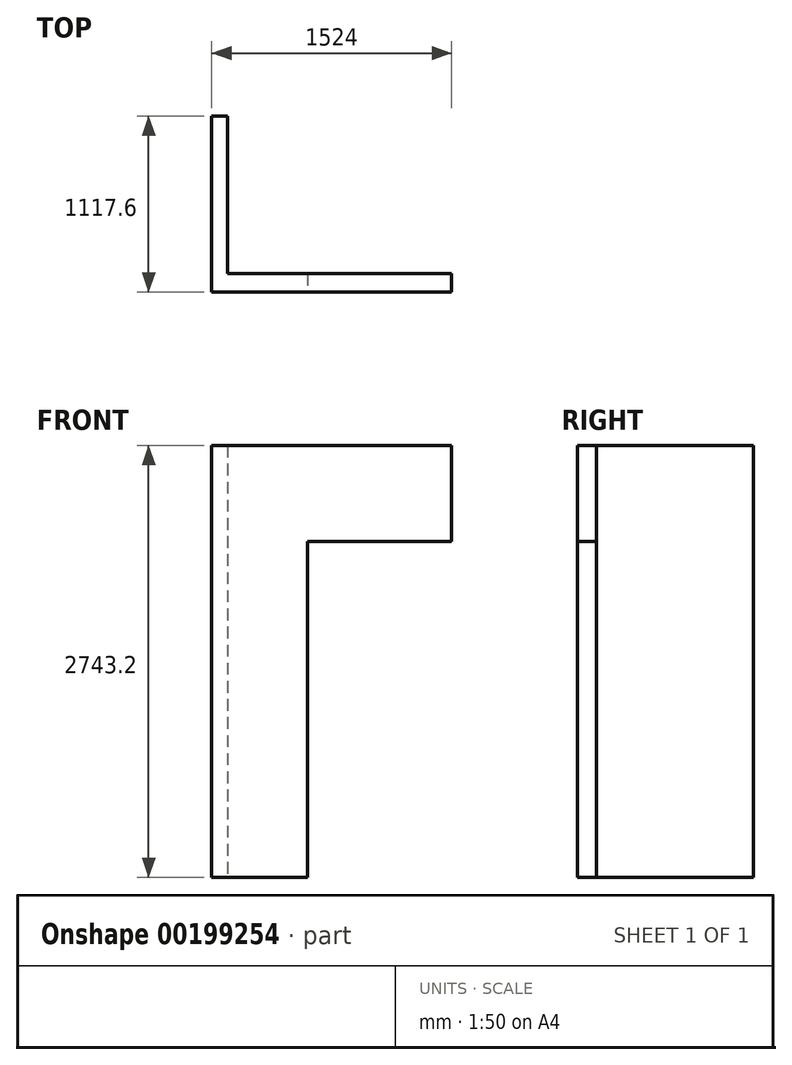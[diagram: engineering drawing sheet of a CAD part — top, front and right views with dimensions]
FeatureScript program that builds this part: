
annotation { "Feature Type Name" : "Feature", "Feature Type Description" : "" }
export const myFeature = defineFeature(function(context is Context, id is Id, definition is map)
    precondition{}
    {
        {
            var Q0;
            Q0=qCreatedBy(makeId("Top.planeOp"),FACE);
            var sketch = newSketch(context, id + "F0", { "sketchPlane" : qUnion([Q0])});
            skLineSegment(sketch, "E0", {"start": v(-2316.67, 229.42) * mm, "end": v(349.93, 229.42) * mm});
            skLineSegment(sketch, "E1", {"start": v(2064.43, -1485.08) * mm, "end": v(2064.43, -2094.68) * mm});
            skArc(sketch, "E2", {"start": v(2064.43, -1485.08) * mm, "mid": v(852.1, -982.92) * mm, "end": v(349.93, 229.42) * mm});
            skArc(sketch, "E3.0", {"start": v(2064.43, -1789.88) * mm, "mid": v(1189.8, -1590.64) * mm, "end": v(487.77, -1032.22) * mm});
            skArc(sketch, "E4.0", {"start": v(2064.43, -2094.68) * mm, "mid": v(1057.78, -1865.36) * mm, "end": v(249.79, -1222.65) * mm});
            skLineSegment(sketch, "E5", {"start": v(-2316.67, 229.42) * mm, "end": v(-2345.78, -77.56) * mm});
            skPoint(sketch, "E6", {"position": v(-2316.67, 229.42) * mm});
            skArc(sketch, "E7", {"start": v(487.77, -1032.22) * mm, "mid": v(-608.98, -137.02) * mm, "end": v(-1976.45, 229.42) * mm});
            skArc(sketch, "E8.0", {"start": v(249.79, -1222.65) * mm, "mid": v(-907.75, -332.21) * mm, "end": v(-2345.78, -77.56) * mm});
            skPoint(sketch, "E9.orphan", {"position": v(-2436.3, -1032.22) * mm});
            skLineSegment(sketch, "E10", {"start": v(-2343.36, -51.95) * mm, "end": v(-2316.67, 229.42) * mm});
            skLineSegment(sketch, "E11", {"start": v(-2291.3, 227.87) * mm, "end": v(-2316.67, 229.42) * mm});
            skLineSegment(sketch, "E12.bottom", {"start": v(2039.03, -1484.9) * mm, "end": v(2064.43, -1484.9) * mm});
            skLineSegment(sketch, "E12.top", {"start": v(2039.03, -1485.08) * mm, "end": v(2064.43, -1485.08) * mm});
            skLineSegment(sketch, "E12.left", {"start": v(2039.03, -1484.9) * mm, "end": v(2039.03, -1485.08) * mm});
            skLineSegment(sketch, "E12.right", {"start": v(2064.43, -1484.9) * mm, "end": v(2064.43, -1485.08) * mm});
            skLineSegment(sketch, "E13.0", {"start": v(2166.03, -1485.08) * mm, "end": v(2166.03, -2094.68) * mm});
            skLineSegment(sketch, "E14", {"start": v(2064.43, -2094.68) * mm, "end": v(2166.03, -2094.68) * mm});
            skLineSegment(sketch, "E15", {"start": v(2166.03, -1485.08) * mm, "end": v(2166.03, -1231.08) * mm});
            skLineSegment(sketch, "E16", {"start": v(2166.03, -2094.68) * mm, "end": v(2166.03, -2361.38) * mm});
            skLineSegment(sketch, "E17", {"start": v(2064.43, -2094.68) * mm, "end": v(2064.43, -2361.38) * mm});
            skLineSegment(sketch, "E18", {"start": v(2166.03, -2361.38) * mm, "end": v(2064.43, -2361.38) * mm});
            skPoint(sketch, "E19.orphan", {"position": v(2064.43, -468.9) * mm});
            skPoint(sketch, "E20", {"position": v(2166.03, -1231.08) * mm});
            skLineSegment(sketch, "E21", {"start": v(2166.03, -1231.08) * mm, "end": v(2166.03, -926.28) * mm});
            skLineSegment(sketch, "E22", {"start": v(2067.25, -926.28) * mm, "end": v(2166.03, -926.28) * mm});
            skPoint(sketch, "E23", {"position": v(2166.03, -1485.08) * mm});
            skPoint(sketch, "E24", {"position": v(2166.03, -2094.68) * mm});
            skArc(sketch, "E25", {"start": v(2166.03, -1231.08) * mm, "mid": v(2140.72, -1070.88) * mm, "end": v(2067.25, -926.28) * mm});
            skArc(sketch, "E26.0", {"start": v(2064.43, -1231.08) * mm, "mid": v(2044.2, -1102.64) * mm, "end": v(1985.51, -986.63) * mm});
            skLineSegment(sketch, "E27", {"start": v(2064.43, -1484.9) * mm, "end": v(2064.43, -1231.08) * mm});
            skLineSegment(sketch, "E28", {"start": v(2067.25, -926.28) * mm, "end": v(1985.51, -986.63) * mm});
            skLineSegment(sketch, "E29", {"start": v(2064.43, -2361.38) * mm, "end": v(2064.43, -3478.98) * mm});
            skLineSegment(sketch, "E30", {"start": v(2064.43, -3478.98) * mm, "end": v(3588.43, -3478.98) * mm});
            skLineSegment(sketch, "E31", {"start": v(2166.03, -2361.38) * mm, "end": v(2166.03, -3478.98) * mm});
            skLineSegment(sketch, "E32", {"start": v(2064.43, -3361.35) * mm, "end": v(3588.43, -3361.35) * mm});
            skLineSegment(sketch, "E33", {"start": v(3588.43, -3478.98) * mm, "end": v(3588.43, -3361.35) * mm});
            skSolve(sketch);
        }
        {
            var Q0;
            {var subQ0=sQuery(id+"F0.wireOp",EDGE,"E18");Q0=makeQuery(id+"F0.imprint","IMPRINT",FACE,{"disambiguationData":[TD([[makeQuery(id+"F0.imprint","IMPRINT",EDGE,{"derivedFrom":subQ0}),1.0]])]});}
            var Q1;
            {var subQ0=sQuery(id+"F0.wireOp",EDGE,"E30");var subQ1=sQuery(id+"F0.wireOp",EDGE,"E29");var subQ2=makeQuery(id+"F0.imprint","INTERSECT",VERTEX,{"derivedFrom":[subQ1,subQ0]});Q1=makeQuery(id+"F0.imprint","IMPRINT",FACE,{"disambiguationData":[TD([[makeQuery(id+"F0.imprint","IMPRINT",EDGE,{"disambiguationData":[TD([[subQ2,1.0]])],"derivedFrom":subQ1}),1.0]])]});}
            var Q2;
            {var subQ0=sQuery(id+"F0.wireOp",EDGE,"E33");Q2=makeQuery(id+"F0.imprint","IMPRINT",FACE,{"disambiguationData":[TD([[makeQuery(id+"F0.imprint","IMPRINT",EDGE,{"derivedFrom":subQ0}),1.0]])]});}
            extrude(context, id + "F1", {"entities" : qUnion([Q0, Q1, Q2]), "depth" : 2743.2 * mm});
        }
        {
            var Q0;
            Q0=makeQuery(id+"F1.opExtrude","SWEPT_FACE",FACE,{"disambiguationData":[OSD([sQuery(id+"F0.wireOp",EDGE,"E30")])]});
            var sketch = newSketch(context, id + "F2", { "sketchPlane" : qUnion([Q0])});
            skLineSegment(sketch, "E34", {"start": v(2064.43, 2743.2) * mm, "end": v(2674.03, 2743.2) * mm});
            skLineSegment(sketch, "E35", {"start": v(2674.03, 2743.2) * mm, "end": v(2674.03, 0) * mm});
            skLineSegment(sketch, "E36", {"start": v(2674.03, 2743.2) * mm, "end": v(3588.43, 2743.2) * mm});
            skLineSegment(sketch, "E37", {"start": v(3588.43, 2743.2) * mm, "end": v(3588.43, 0) * mm});
            skLineSegment(sketch, "E38", {"start": v(3588.43, 0) * mm, "end": v(2674.03, 0) * mm});
            skPoint(sketch, "E39", {"position": v(3588.43, 2133.6) * mm});
            skLineSegment(sketch, "E40", {"start": v(3588.43, 2133.6) * mm, "end": v(2674.03, 2133.6) * mm});
            skSolve(sketch);
        }
        {
            var Q0;
            {var subQ0=sQuery(id+"F2.wireOp",EDGE,"E38");Q0=makeQuery(id+"F2.imprint","IMPRINT",FACE,{"disambiguationData":[TD([[makeQuery(id+"F2.imprint","IMPRINT",EDGE,{"derivedFrom":subQ0}),1.0]])]});}
            extrude(context, id + "F3", {"entities" : qUnion([Q0]), "operationType" : NewBodyOperationType.REMOVE, "endBound" : BoundingType.THROUGH_ALL, "oppositeDirection" : true, "depth" : 101.6 * mm});
        }
    });
